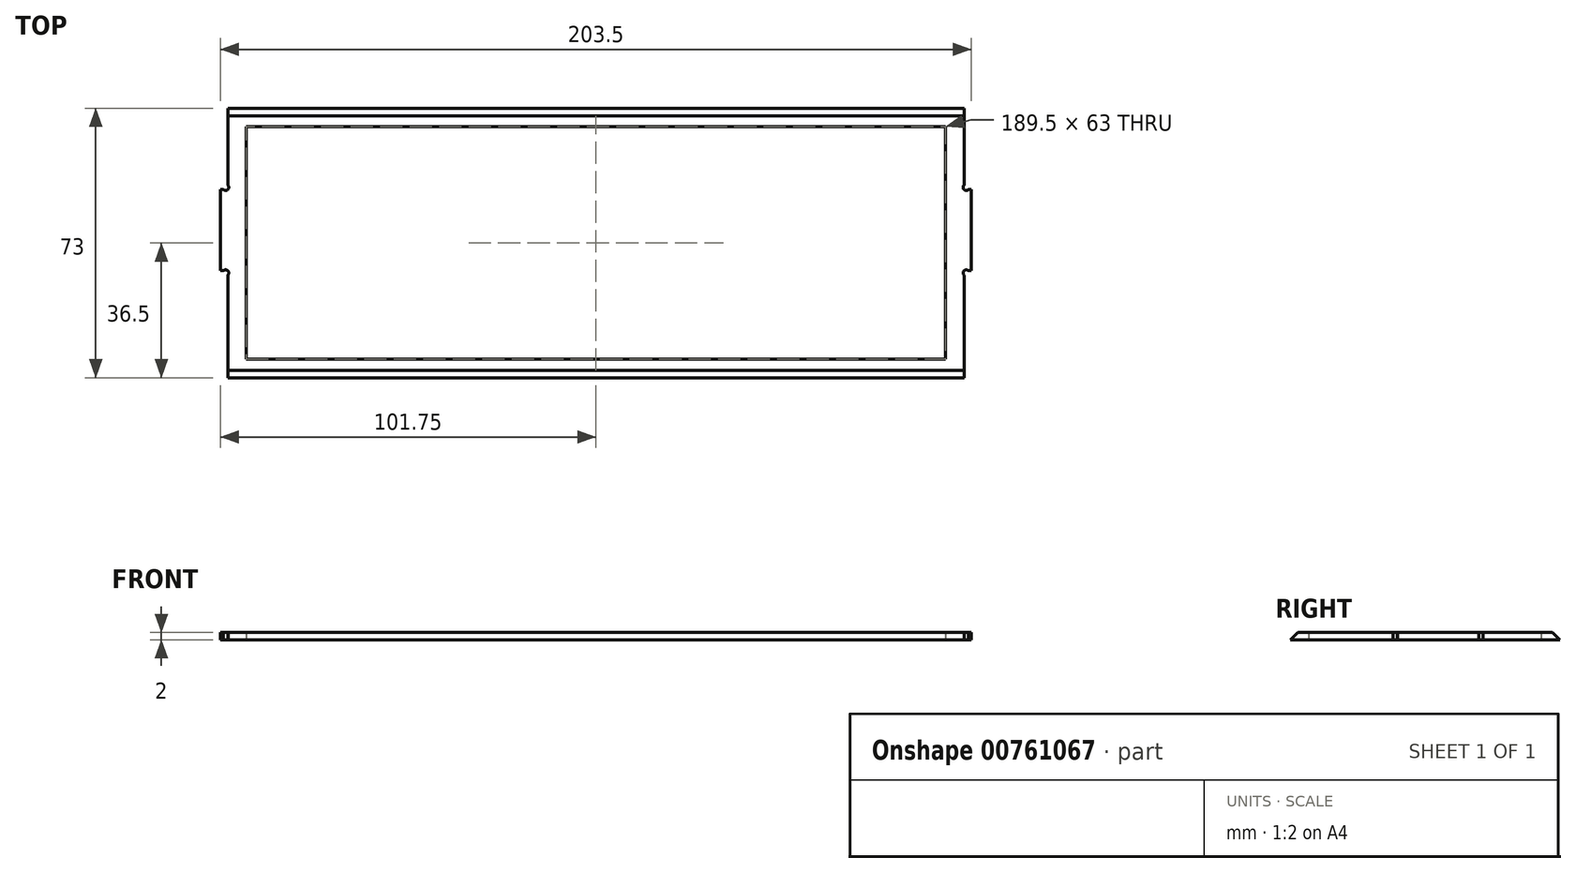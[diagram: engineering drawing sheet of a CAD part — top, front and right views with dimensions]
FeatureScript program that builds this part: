
annotation { "Feature Type Name" : "Feature", "Feature Type Description" : "" }
export const myFeature = defineFeature(function(context is Context, id is Id, definition is map)
    precondition{}
    {
        {
            var Q0;
            Q0=qCreatedBy(makeId("Top.planeOp"),FACE);
            var sketch = newSketch(context, id + "F0", { "sketchPlane" : qUnion([Q0])});
            skLineSegment(sketch, "E0", {"start": v(-100, 51) * mm, "end": v(-100, 29) * mm});
            skLineSegment(sketch, "E1", {"start": v(103.5, 51) * mm, "end": v(103.5, 29) * mm});
            skLineSegment(sketch, "E2", {"start": v(-98, 73) * mm, "end": v(101.5, 73) * mm});
            skLineSegment(sketch, "E3", {"start": v(101.5, 0) * mm, "end": v(-98, 0) * mm});
            skLineSegment(sketch, "E4", {"start": v(-93, 68) * mm, "end": v(96.5, 68) * mm});
            skLineSegment(sketch, "E5", {"start": v(96.5, 68) * mm, "end": v(96.5, 5) * mm});
            skLineSegment(sketch, "E6", {"start": v(96.5, 5) * mm, "end": v(-93, 5) * mm});
            skLineSegment(sketch, "E7", {"start": v(-93, 5) * mm, "end": v(-93, 68) * mm});
            skLineSegment(sketch, "E8", {"start": v(-99.2, 29) * mm, "end": v(-100, 29) * mm});
            skLineSegment(sketch, "E9", {"start": v(-100, 51) * mm, "end": v(-99.2, 51) * mm});
            skArc(sketch, "E10", {"start": v(-99.2, 51) * mm, "mid": v(-98, 51) * mm, "end": v(-98, 52.2) * mm});
            skLineSegment(sketch, "E11", {"start": v(-98, 73) * mm, "end": v(-98, 52.2) * mm});
            skArc(sketch, "E12", {"start": v(-98, 27.8) * mm, "mid": v(-98, 29) * mm, "end": v(-99.2, 29) * mm});
            skLineSegment(sketch, "E13", {"start": v(-98, 27.8) * mm, "end": v(-98, 0) * mm});
            skLineSegment(sketch, "E14", {"start": v(103.5, 51) * mm, "end": v(102.7, 51) * mm});
            skArc(sketch, "E15", {"start": v(101.5, 52.2) * mm, "mid": v(101.5, 51) * mm, "end": v(102.7, 51) * mm});
            skLineSegment(sketch, "E16", {"start": v(101.5, 52.2) * mm, "end": v(101.5, 73) * mm});
            skLineSegment(sketch, "E17", {"start": v(103.5, 29) * mm, "end": v(102.7, 29) * mm});
            skArc(sketch, "E18", {"start": v(102.7, 29) * mm, "mid": v(101.5, 29) * mm, "end": v(101.5, 27.8) * mm});
            skLineSegment(sketch, "E19", {"start": v(101.5, 27.8) * mm, "end": v(101.5, 0) * mm});
            skSolve(sketch);
        }
        {
            var Q0;
            Q0 = qSketchRegion(id + "F0", true);
            extrude(context, id + "F1", {"entities" : qUnion([Q0]), "depth" : 2 * mm, "offsetDistance" : 25 * mm});
        }
        {
            var Q0;
            Q0=makeQuery(id+"F1.opExtrude","CAP_EDGE",EDGE,{"disambiguationData":[OSD([sQuery(id+"F0.wireOp",EDGE,"E3")])],"isStart":false});
            chamfer(context, id + "F2", {"entities" : qUnion([Q0]), "width" : 2 * mm, "tangentPropagation" : true});
        }
        {
            var Q0;
            Q0=makeQuery(id+"F1.opExtrude","CAP_EDGE",EDGE,{"disambiguationData":[OSD([sQuery(id+"F0.wireOp",EDGE,"E2")])],"isStart":false});
            chamfer(context, id + "F3", {"entities" : qUnion([Q0]), "width" : 2 * mm, "tangentPropagation" : true});
        }
    });
